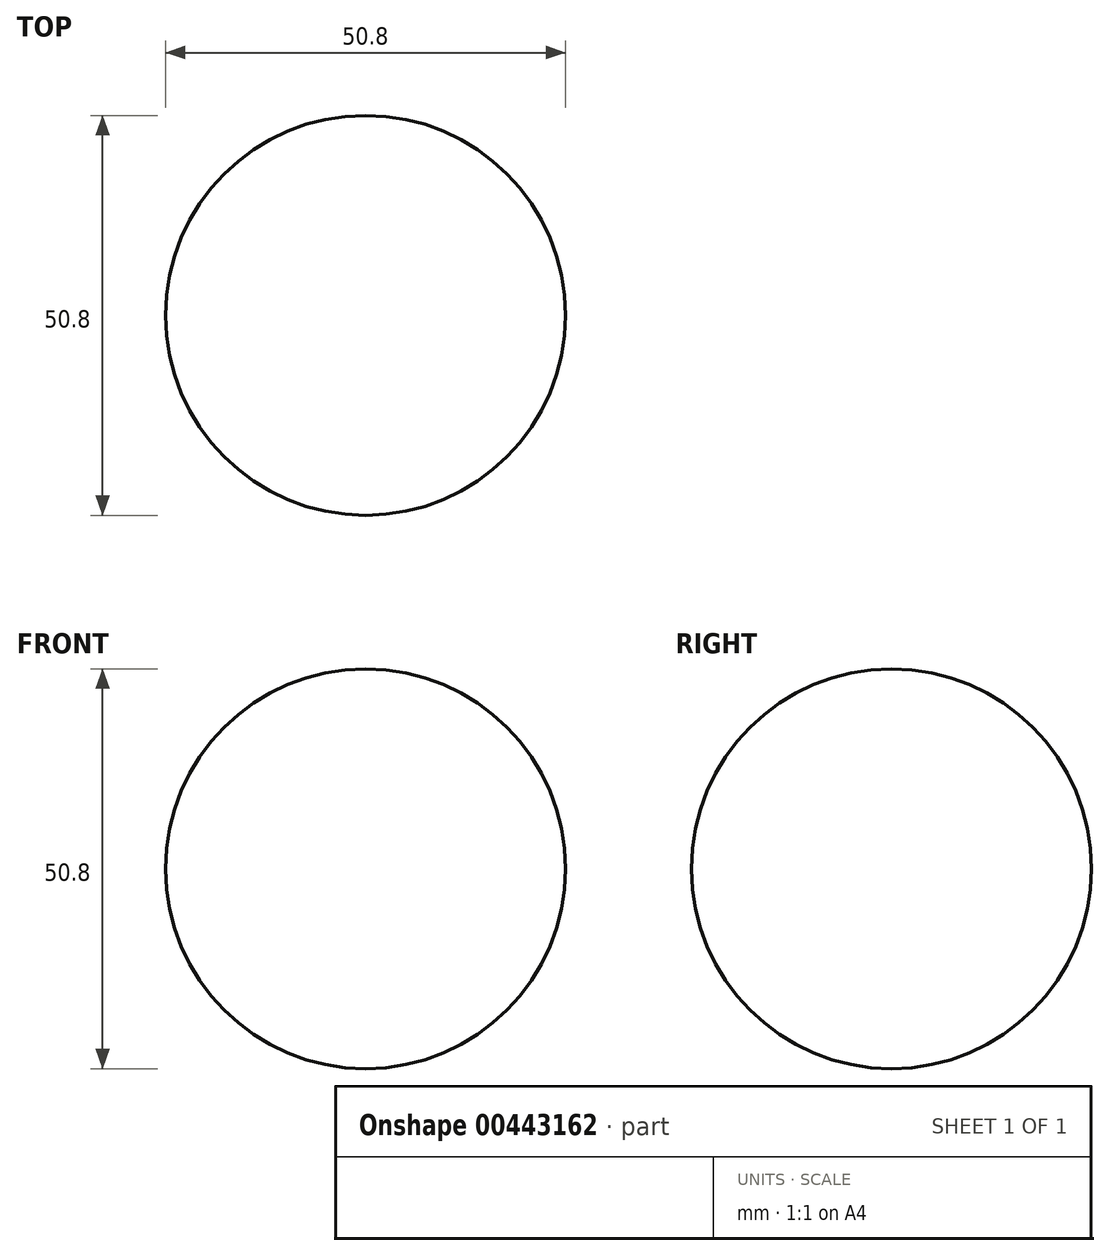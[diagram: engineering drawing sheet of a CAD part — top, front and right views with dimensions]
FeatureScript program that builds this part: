
annotation { "Feature Type Name" : "Feature", "Feature Type Description" : "" }
export const myFeature = defineFeature(function(context is Context, id is Id, definition is map)
    precondition{}
    {
        {
            var Q0;
            Q0=qCreatedBy(makeId("Front.planeOp"),FACE);
            var sketch = newSketch(context, id + "F0", { "sketchPlane" : qUnion([Q0])});
            skLineSegment(sketch, "E0", {"start": v(0, 0) * mm, "end": v(0, -50.8) * mm});
            skArc(sketch, "E1", {"start": v(0, 0) * mm, "mid": v(25.4, -25.4) * mm, "end": v(0, -50.8) * mm});
            skLineSegment(sketch, "E2", {"start": v(44.9, -25.4) * mm, "end": v(-52.26, -25.4) * mm, "construction": true});
            skPoint(sketch, "E3", {"position": v(0, -50.8) * mm});
            skSolve(sketch);
        }
        {
            var Q0;
            Q0=sQuery(id+"F0.wireOp",EDGE,"E1");
            var Q1;
            Q1=sQuery(id+"F0.wireOp",EDGE,"E0");
            revolve(context, id + "F1", {"bodyType" : ToolBodyType.SURFACE, "surfaceEntities" : qUnion([Q0]), "axis" : qUnion([Q1]), "revolveType" : RevolveType.FULL});
        }
    });
